# Revit family: Thermostatic_Trim-American_Standard-Delancey-TU052740_Series
name_source: partatom
category: Plumbing Fixtures
revit_build: Autodesk Revit 2014 (Build: 20130308_1515(x64)
units: mm (PartAtom-declared; Revit-internal decimal feet)

## types (4) — shared parameters
ADA Compliant = Yes
Assembly Code = D2020300
CW Connection = Yes
CWFU = 3
Cold Water Connection Diameter = 1/2"
Cold Water Connection Radius = 1/4"
Default Elevation = 44"
Description = Delancey Thermostat Trim
HW Connection = Yes
HWFU = 3
Height = 8"
Hot Water Connection Diameter = 1"
Hot Water Connection Radius = 1/4"
Installation Type = Wall Mounted
Length = 4 3/16"
Manufacturer = American Standard
Price = Prices may vary. Please consult Manufacturer Representative for most up-to-date price list.
URL = https://www.americanstandard-us.com
Vent Connection = No
WFU = 4
Warranty Information = Limited Lifetime Function and Finish Warranty
Waste Connection = No
Water Connection Diameter = 1/2"
Water Connection Radius = 1/4"
Width = 8"

## per-type parameters (varying)
| type | Finish | Material |
| T052740.002 | Metal-American Standard-002-Polished Chrome | Metal-American Standard-002-Polished Chrome |
| T052740.295 | Metal-American Standard-295-Brushed Nickel | Metal-American Standard-295-Brushed Nickel |
| T052740.013 | Metal-American Standard-013-Polished Nickel | Metal-American Standard-013-Polished Nickel |
| T052740.278 | Metal-American Standard-278-Legacy Bronze | Metal-American Standard-278-Legacy Bronze |

note: column(s) folded — value = type name in every type: Model

## geometry (parser evidence)
native form markers: Sweep x1
no freeform markers — native parametric forms only
